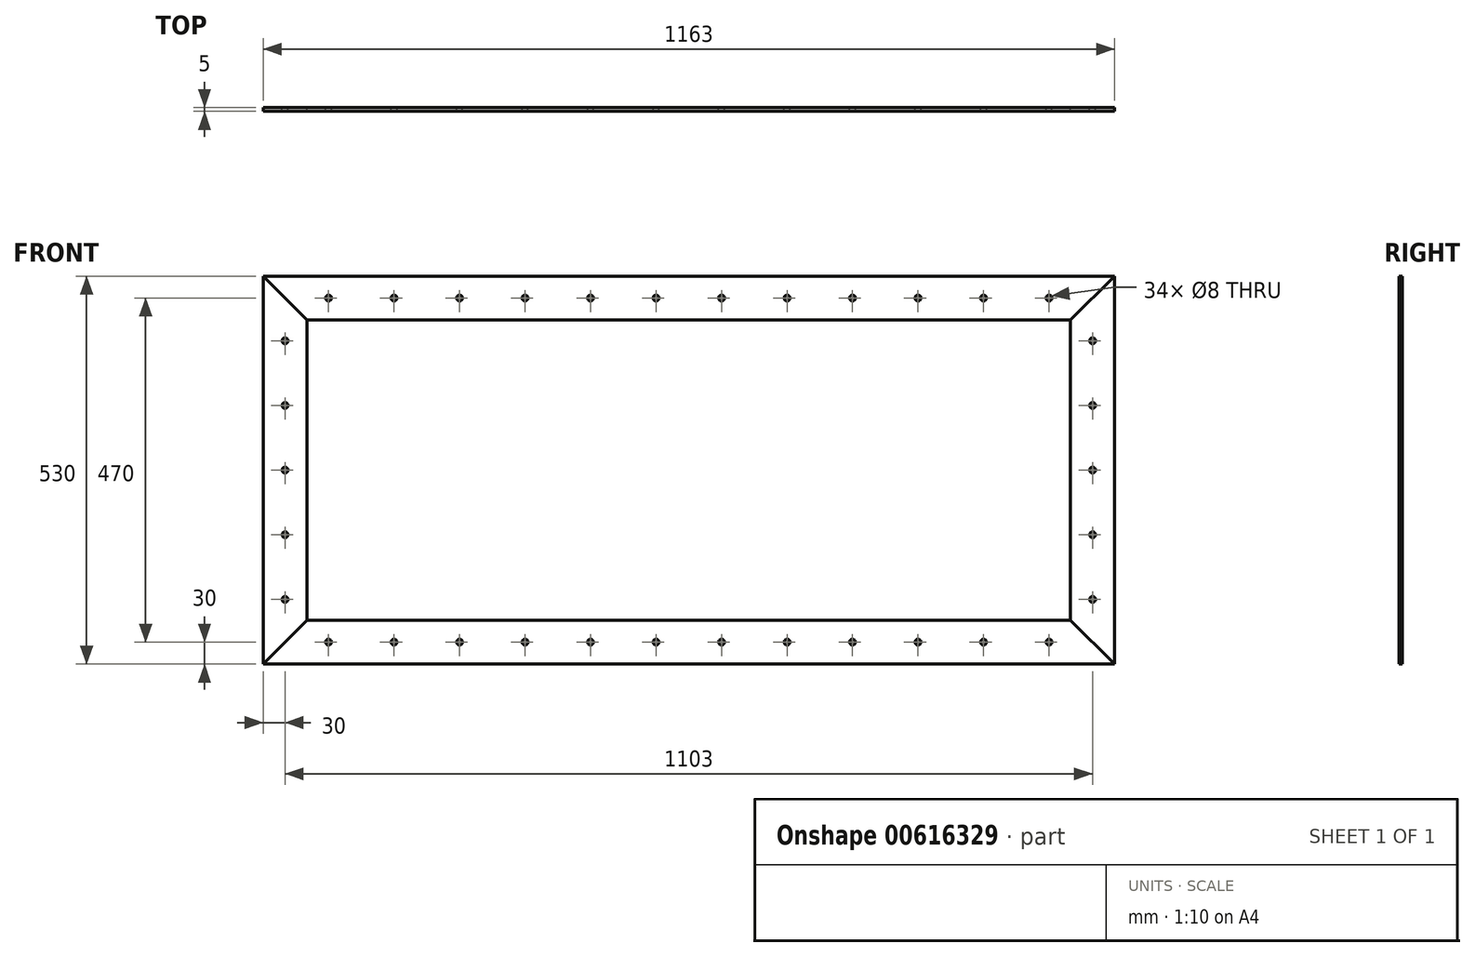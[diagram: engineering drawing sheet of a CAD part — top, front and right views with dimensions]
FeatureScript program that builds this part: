
annotation { "Feature Type Name" : "Feature", "Feature Type Description" : "" }
export const myFeature = defineFeature(function(context is Context, id is Id, definition is map)
    precondition{}
    {
        {
            var Q0;
            Q0=qCreatedBy(makeId("Front.planeOp"),FACE);
            var sketch = newSketch(context, id + "F0", { "sketchPlane" : qUnion([Q0])});
            skLineSegment(sketch, "E0", {"start": v(-581.5, -60) * mm, "end": v(581.5, -60) * mm});
            skLineSegment(sketch, "E1", {"start": v(581.5, -60) * mm, "end": v(521.5, 0) * mm});
            skLineSegment(sketch, "E2", {"start": v(521.5, 0) * mm, "end": v(-521.5, 0) * mm});
            skLineSegment(sketch, "E3", {"start": v(-521.5, 0) * mm, "end": v(-581.5, -60) * mm});
            skCircle(sketch, "E4", {"center": v(492.04, -30) * mm, "radius": 4 * mm});
            skPoint(sketch, "E4.centerSnap0", {"position": v(551.5, -30) * mm});
            skCircle(sketch, "E5.1.0.0", {"center": v(402.58, -30) * mm, "radius": 4 * mm});
            skCircle(sketch, "E5.2.0.0", {"center": v(313.12, -30) * mm, "radius": 4 * mm});
            skLineSegment(sketch, "E5.direction1", {"start": v(492.04, -30) * mm, "end": v(402.58, -30) * mm, "construction": true});
            skCircle(sketch, "E6.0.3.0", {"center": v(223.66, -30) * mm, "radius": 4 * mm});
            skCircle(sketch, "E6.0.4.0", {"center": v(134.2, -30) * mm, "radius": 4 * mm});
            skCircle(sketch, "E6.0.5.0", {"center": v(44.74, -30) * mm, "radius": 4 * mm});
            skCircle(sketch, "E6.0.6.0", {"center": v(-44.72, -30) * mm, "radius": 4 * mm});
            skCircle(sketch, "E6.0.7.0", {"center": v(-134.18, -30) * mm, "radius": 4 * mm});
            skCircle(sketch, "E6.0.8.0", {"center": v(-223.64, -30) * mm, "radius": 4 * mm});
            skCircle(sketch, "E6.0.9.0", {"center": v(-313.1, -30) * mm, "radius": 4 * mm});
            skCircle(sketch, "E6.0.10.0", {"center": v(-402.56, -30) * mm, "radius": 4 * mm});
            skCircle(sketch, "E7.0.11.0", {"center": v(-492.02, -30) * mm, "radius": 4 * mm});
            skLineSegment(sketch, "E8", {"start": v(-144.64, 205) * mm, "end": v(132.3, 205) * mm});
            skLineSegment(sketch, "E9.MirrorCS", {"start": v(-581.5, 470) * mm, "end": v(581.5, 470) * mm});
            skLineSegment(sketch, "E10.MirrorCS", {"start": v(521.5, 410) * mm, "end": v(-521.5, 410) * mm});
            skLineSegment(sketch, "E11.MirrorCS", {"start": v(-521.5, 410) * mm, "end": v(-581.5, 470) * mm});
            skLineSegment(sketch, "E12.MirrorCS", {"start": v(581.5, 470) * mm, "end": v(521.5, 410) * mm});
            skCircle(sketch, "E13.MirrorC", {"center": v(402.58, 440) * mm, "radius": 4 * mm});
            skCircle(sketch, "E14.MirrorC", {"center": v(313.12, 440) * mm, "radius": 4 * mm});
            skCircle(sketch, "E15.MirrorC", {"center": v(223.66, 440) * mm, "radius": 4 * mm});
            skCircle(sketch, "E16.MirrorC", {"center": v(134.2, 440) * mm, "radius": 4 * mm});
            skCircle(sketch, "E17.MirrorC", {"center": v(44.74, 440) * mm, "radius": 4 * mm});
            skCircle(sketch, "E18.MirrorC", {"center": v(-44.72, 440) * mm, "radius": 4 * mm});
            skCircle(sketch, "E19.MirrorC", {"center": v(-134.18, 440) * mm, "radius": 4 * mm});
            skCircle(sketch, "E20.MirrorC", {"center": v(-223.64, 440) * mm, "radius": 4 * mm});
            skCircle(sketch, "E21.MirrorC", {"center": v(-313.1, 440) * mm, "radius": 4 * mm});
            skCircle(sketch, "E22.MirrorC", {"center": v(-402.56, 440) * mm, "radius": 4 * mm});
            skCircle(sketch, "E23.MirrorC", {"center": v(-492.02, 440) * mm, "radius": 4 * mm});
            skCircle(sketch, "E24.MirrorC", {"center": v(492.04, 440) * mm, "radius": 4 * mm});
            skSolve(sketch);
        }
        {
            var Q0;
            Q0=qCreatedBy(makeId("Front.planeOp"),FACE);
            var sketch = newSketch(context, id + "F1", { "sketchPlane" : qUnion([Q0])});
            skLineSegment(sketch, "E25", {"start": v(581.5, -60) * mm, "end": v(581.5, 470) * mm});
            skLineSegment(sketch, "E26", {"start": v(581.5, 470) * mm, "end": v(521.5, 410) * mm});
            skLineSegment(sketch, "E27", {"start": v(521.5, 410) * mm, "end": v(521.5, 0) * mm});
            skLineSegment(sketch, "E28", {"start": v(521.5, 0) * mm, "end": v(581.5, -60) * mm});
            skCircle(sketch, "E29", {"center": v(551.5, 28.33) * mm, "radius": 4 * mm});
            skPoint(sketch, "E29.centerSnap0", {"position": v(551.5, -30) * mm});
            skCircle(sketch, "E30.0.1.0", {"center": v(551.5, 116.66) * mm, "radius": 4 * mm});
            skCircle(sketch, "E30.0.2.0", {"center": v(551.5, 205) * mm, "radius": 4 * mm});
            skCircle(sketch, "E30.0.3.0", {"center": v(551.5, 293.32) * mm, "radius": 4 * mm});
            skCircle(sketch, "E30.0.4.0", {"center": v(551.5, 381.65) * mm, "radius": 4 * mm});
            skLineSegment(sketch, "E30.direction1", {"start": v(551.5, 28.33) * mm, "end": v(576.5, 28.33) * mm, "construction": true});
            skLineSegment(sketch, "E30.direction2", {"start": v(551.5, 28.33) * mm, "end": v(551.5, 116.66) * mm, "construction": true});
            skLineSegment(sketch, "E31", {"start": v(0, 282.88) * mm, "end": v(0, 129.84) * mm});
            skLineSegment(sketch, "E32.MirrorCS", {"start": v(-581.5, -60) * mm, "end": v(-581.5, 470) * mm});
            skLineSegment(sketch, "E33.MirrorCS", {"start": v(-521.5, 410) * mm, "end": v(-521.5, 0) * mm});
            skCircle(sketch, "E34.MirrorC", {"center": v(-551.5, 116.66) * mm, "radius": 4 * mm});
            skCircle(sketch, "E35.MirrorC", {"center": v(-551.5, 28.33) * mm, "radius": 4 * mm});
            skLineSegment(sketch, "E36.MirrorCS", {"start": v(-581.5, 470) * mm, "end": v(-521.5, 410) * mm});
            skCircle(sketch, "E37.MirrorC", {"center": v(-551.5, 293.32) * mm, "radius": 4 * mm});
            skCircle(sketch, "E38.MirrorC", {"center": v(-551.5, 381.65) * mm, "radius": 4 * mm});
            skCircle(sketch, "E39.MirrorC", {"center": v(-551.5, 205) * mm, "radius": 4 * mm});
            skLineSegment(sketch, "E40.MirrorCS", {"start": v(-521.5, 0) * mm, "end": v(-581.5, -60) * mm});
            skSolve(sketch);
        }
        {
            var Q0;
            Q0=makeQuery(id+"F0.imprint","IMPRINT",FACE,{"disambiguationData":[TD([[makeQuery(id+"F0.imprint","IMPRINT",EDGE,{"derivedFrom":sQuery(id+"F0.wireOp",EDGE,"E0")}),1.0]])]});
            var Q1;
            Q1=makeQuery(id+"F1.imprint","IMPRINT",FACE,{"disambiguationData":[TD([[makeQuery(id+"F1.imprint","IMPRINT",EDGE,{"derivedFrom":sQuery(id+"F1.wireOp",EDGE,"E32.MirrorCS")}),-1.0]])]});
            var Q2;
            Q2=makeQuery(id+"F0.imprint","IMPRINT",FACE,{"disambiguationData":[TD([[makeQuery(id+"F0.imprint","IMPRINT",EDGE,{"derivedFrom":sQuery(id+"F0.wireOp",EDGE,"E9.MirrorCS")}),-1.0]])]});
            var Q3;
            Q3=makeQuery(id+"F1.imprint","IMPRINT",FACE,{"disambiguationData":[TD([[makeQuery(id+"F1.imprint","IMPRINT",EDGE,{"derivedFrom":sQuery(id+"F1.wireOp",EDGE,"E25")}),1.0]])]});
            extrude(context, id + "F2", {"entities" : qUnion([Q0, Q1, Q2, Q3]), "endBound" : BoundingType.SYMMETRIC, "depth" : 5 * mm, "offsetDistance" : 25 * mm});
        }
    });
